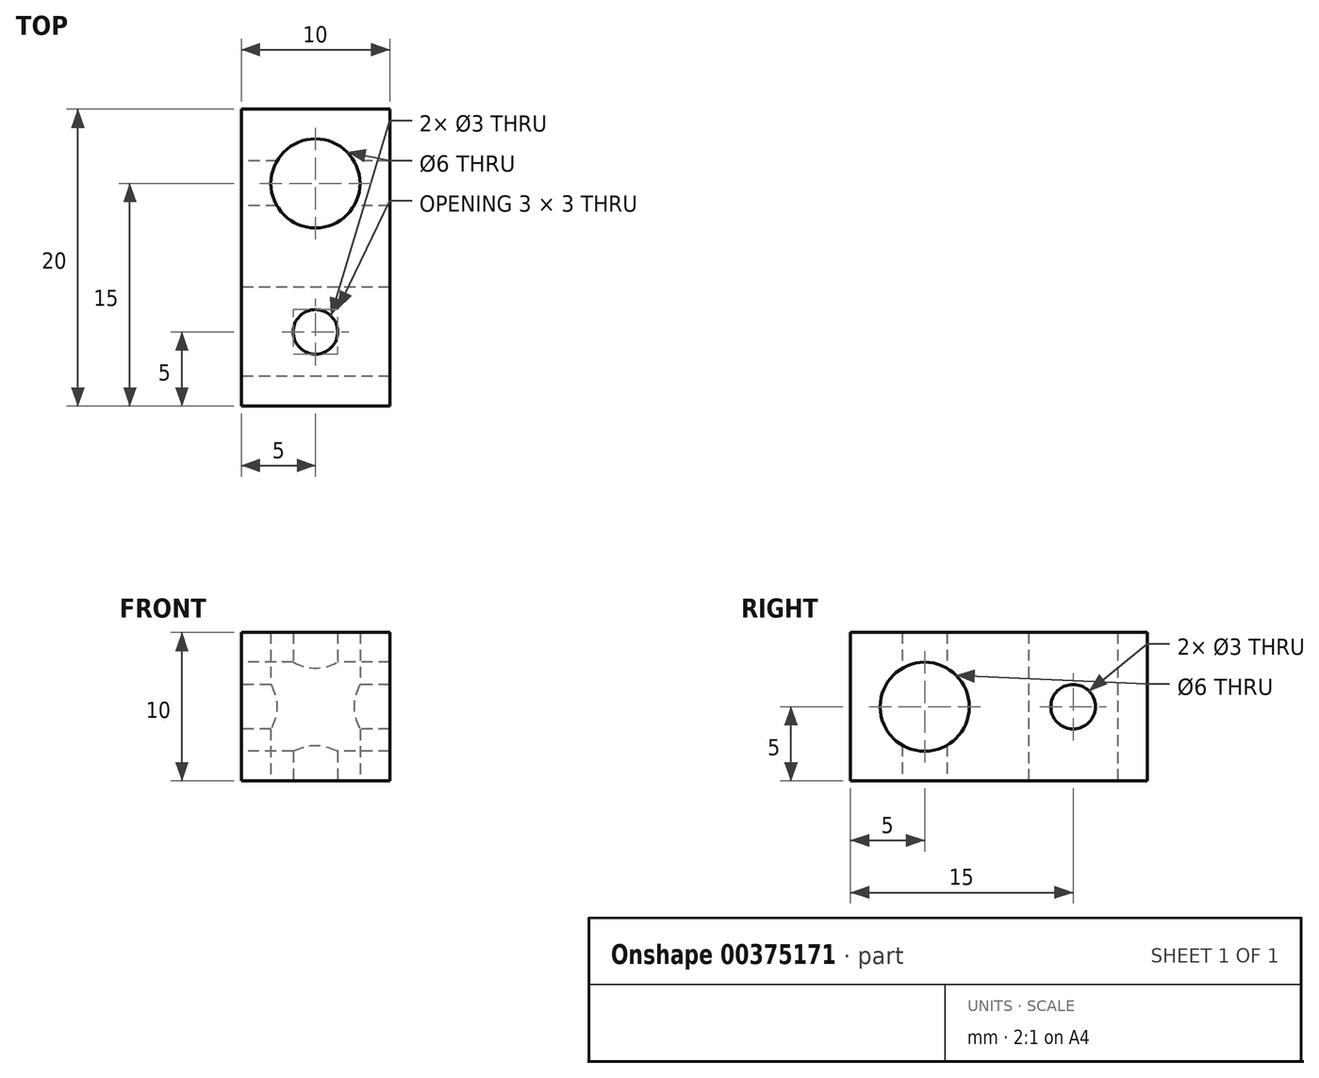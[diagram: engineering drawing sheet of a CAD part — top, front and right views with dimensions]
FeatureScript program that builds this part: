
annotation { "Feature Type Name" : "Feature", "Feature Type Description" : "" }
export const myFeature = defineFeature(function(context is Context, id is Id, definition is map)
    precondition{}
    {
        {
            var Q0;
            Q0=qCreatedBy(makeId("Top.planeOp"),FACE);
            var sketch = newSketch(context, id + "F0", { "sketchPlane" : qUnion([Q0])});
            skLineSegment(sketch, "E0.bottom", {"start": v(5, 10) * mm, "end": v(-5, 10) * mm});
            skLineSegment(sketch, "E0.top", {"start": v(5, -10) * mm, "end": v(-5, -10) * mm});
            skLineSegment(sketch, "E0.left", {"start": v(5, 10) * mm, "end": v(5, -10) * mm});
            skLineSegment(sketch, "E0.right", {"start": v(-5, 10) * mm, "end": v(-5, -10) * mm});
            skPoint(sketch, "E0.middle", {"position": v(0, 0) * mm});
            skCircle(sketch, "E1", {"center": v(0, 5) * mm, "radius": 3 * mm});
            skCircle(sketch, "E2", {"center": v(0, -5) * mm, "radius": 1.5 * mm});
            skSolve(sketch);
        }
        {
            var Q0;
            Q0=makeQuery(id+"F0.imprint","IMPRINT",FACE,{"disambiguationData":[TD([[makeQuery(id+"F0.imprint","IMPRINT",EDGE,{"derivedFrom":sQuery(id+"F0.wireOp",EDGE,"E0.bottom")}),1.0]])]});
            extrude(context, id + "F1", {"entities" : qUnion([Q0]), "depth" : 10 * mm});
        }
        {
            var Q0;
            Q0=makeQuery(id+"F1.opExtrude","SWEPT_FACE",FACE,{"disambiguationData":[OSD([sQuery(id+"F0.wireOp",EDGE,"E0.right")])]});
            var sketch = newSketch(context, id + "F2", { "sketchPlane" : qUnion([Q0])});
            skCircle(sketch, "E3", {"center": v(-5, 5) * mm, "radius": 1.5 * mm});
            skCircle(sketch, "E4", {"center": v(5, 5) * mm, "radius": 3 * mm});
            skSolve(sketch);
        }
        {
            var Q0;
            Q0=makeQuery(id+"F2.imprint","IMPRINT",FACE,{"disambiguationData":[TD([[makeQuery(id+"F2.imprint","IMPRINT",EDGE,{"derivedFrom":sQuery(id+"F2.wireOp",EDGE,"E4")}),1.0]])]});
            var Q1;
            Q1=makeQuery(id+"F2.imprint","IMPRINT",FACE,{"disambiguationData":[TD([[makeQuery(id+"F2.imprint","IMPRINT",EDGE,{"derivedFrom":sQuery(id+"F2.wireOp",EDGE,"E3")}),1.0]])]});
            extrude(context, id + "F3", {"entities" : qUnion([Q0, Q1]), "operationType" : NewBodyOperationType.REMOVE, "oppositeDirection" : true, "depth" : 25 * mm});
        }
    });
